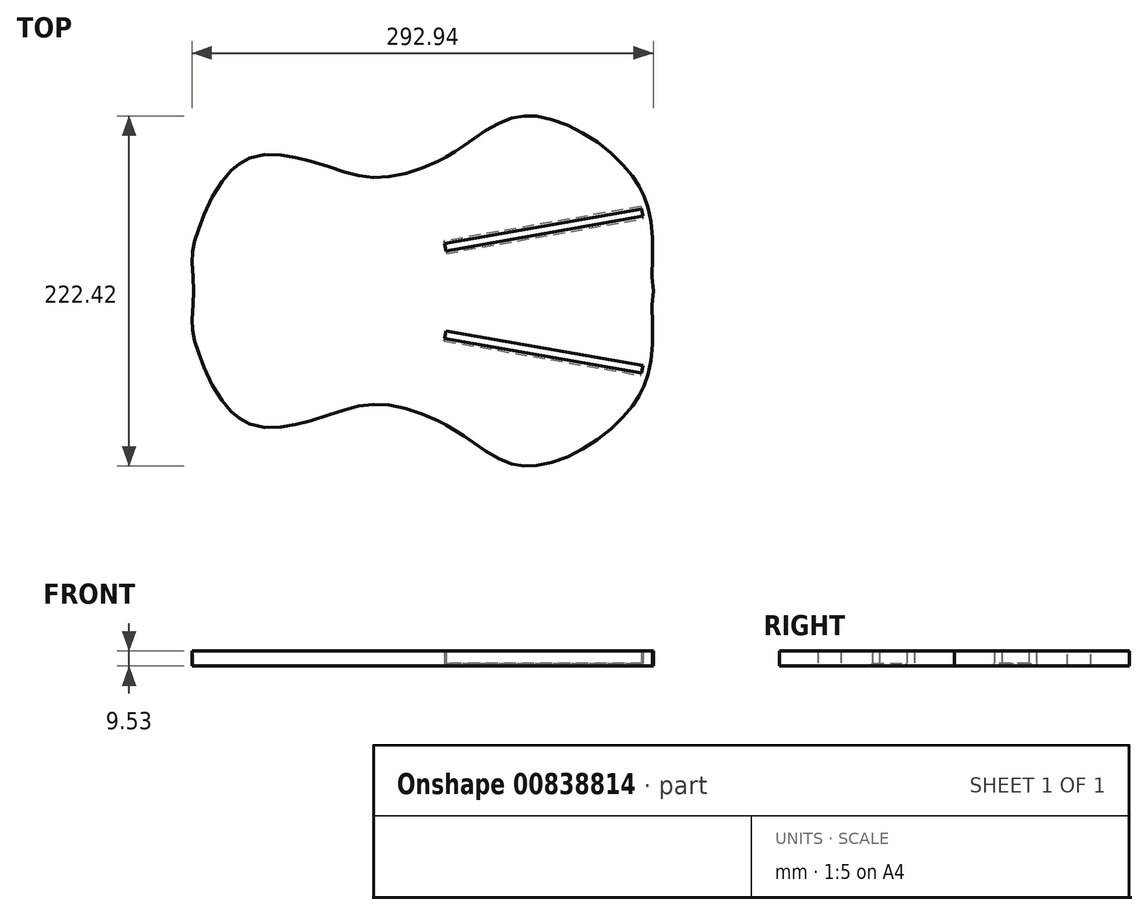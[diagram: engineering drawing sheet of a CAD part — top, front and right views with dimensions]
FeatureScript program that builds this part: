
annotation { "Feature Type Name" : "Feature", "Feature Type Description" : "" }
export const myFeature = defineFeature(function(context is Context, id is Id, definition is map)
    precondition{}
    {
        {
            var Q0;
            Q0=qCreatedBy(makeId("Top.planeOp"),FACE);
            var sketch = newSketch(context, id + "F0", { "sketchPlane" : qUnion([Q0])});
            skFitSpline(sketch, "E0.0", {"points": [v(-120.65, 0) * mm, v(-120.65, 2.86) * mm, v(-120.78, 7.78) * mm, v(-121.14, 13.33) * mm, v(-121.46, 17.64) * mm, v(-121.52, 20.68) * mm, v(-121.36, 23.19) * mm, v(-121.13, 25.21) * mm, v(-120.73, 27.5) * mm, v(-120.15, 30.12) * mm, v(-119.4, 33.04) * mm, v(-118.46, 36.2) * mm, v(-117.36, 39.56) * mm, v(-115.68, 44.24) * mm, v(-113.2, 50.35) * mm, v(-109.68, 57.75) * mm, v(-105.67, 64.87) * mm, v(-102, 70.27) * mm, v(-98.9, 74.1) * mm, v(-96.5, 76.7) * mm, v(-94.47, 78.57) * mm, v(-92.83, 79.9) * mm, v(-91.16, 81.11) * mm, v(-89.05, 82.43) * mm, v(-85.6, 84.16) * mm, v(-81.13, 85.67) * mm, v(-75.54, 86.57) * mm, v(-69.76, 86.7) * mm, v(-63.85, 86.21) * mm, v(-58.88, 85.4) * mm, v(-54.92, 84.57) * mm, v(-51, 83.66) * mm, v(-44.2, 81.86) * mm, v(-36.73, 79.5) * mm, v(-29.7, 77.2) * mm, v(-24.7, 75.6) * mm, v(-19.97, 74.2) * mm, v(-15.38, 73.09) * mm, v(-10.74, 72.3) * mm, v(-5.92, 71.95) * mm, v(-0.77, 72.07) * mm, v(4.85, 72.72) * mm, v(10.87, 73.9) * mm, v(17.2, 75.57) * mm, v(23.74, 77.73) * mm, v(30.39, 80.39) * mm, v(35.92, 83) * mm, v(40.3, 85.33) * mm, v(43.54, 87.2) * mm, v(46.72, 89.17) * mm, v(49.83, 91.23) * mm, v(52.87, 93.34) * mm, v(56.87, 96.16) * mm, v(61.79, 99.64) * mm, v(67.68, 103.5) * mm, v(73.66, 106.8) * mm, v(79.84, 109.33) * mm, v(85.24, 110.64) * mm, v(89.81, 111.12) * mm, v(94.57, 111.17) * mm, v(101, 110.4) * mm, v(109.24, 108.22) * mm, v(117.73, 104.9) * mm, v(126.24, 100.58) * mm, v(134.55, 95.38) * mm, v(142.43, 89.43) * mm, v(149.65, 82.9) * mm, v(154.94, 77.07) * mm, v(158.62, 72.27) * mm, v(161.1, 68.6) * mm, v(163.24, 64.92) * mm, v(165.04, 61.22) * mm, v(166.54, 57.47) * mm, v(168.16, 52.43) * mm, v(169.57, 46.04) * mm, v(170.5, 38.28) * mm, v(170.98, 27.85) * mm, v(170.75, 14.8) * mm, v(170.94, 4.63) * mm, v(171.47, -0.34) * mm]});
            skFitSpline(sketch, "E1.0", {"points": [v(-120.65, 0) * mm, v(-120.65, -2.86) * mm, v(-120.78, -7.78) * mm, v(-121.14, -13.33) * mm, v(-121.46, -17.64) * mm, v(-121.52, -20.68) * mm, v(-121.36, -23.19) * mm, v(-121.13, -25.21) * mm, v(-120.73, -27.5) * mm, v(-120.15, -30.12) * mm, v(-119.4, -33.04) * mm, v(-118.46, -36.2) * mm, v(-117.36, -39.56) * mm, v(-115.68, -44.24) * mm, v(-113.2, -50.35) * mm, v(-109.68, -57.75) * mm, v(-105.67, -64.87) * mm, v(-102, -70.27) * mm, v(-98.9, -74.1) * mm, v(-96.5, -76.7) * mm, v(-94.47, -78.57) * mm, v(-92.83, -79.9) * mm, v(-91.16, -81.11) * mm, v(-89.05, -82.43) * mm, v(-85.6, -84.16) * mm, v(-81.13, -85.67) * mm, v(-75.54, -86.57) * mm, v(-69.76, -86.7) * mm, v(-63.85, -86.21) * mm, v(-58.88, -85.4) * mm, v(-54.92, -84.57) * mm, v(-51, -83.66) * mm, v(-44.2, -81.86) * mm, v(-36.73, -79.5) * mm, v(-29.7, -77.2) * mm, v(-24.7, -75.6) * mm, v(-19.97, -74.2) * mm, v(-15.38, -73.09) * mm, v(-10.74, -72.3) * mm, v(-5.92, -71.95) * mm, v(-0.77, -72.07) * mm, v(4.85, -72.72) * mm, v(10.87, -73.9) * mm, v(17.2, -75.57) * mm, v(23.74, -77.73) * mm, v(30.39, -80.39) * mm, v(35.92, -83) * mm, v(40.3, -85.33) * mm, v(43.54, -87.2) * mm, v(46.72, -89.17) * mm, v(49.83, -91.23) * mm, v(52.87, -93.34) * mm, v(56.87, -96.16) * mm, v(61.79, -99.64) * mm, v(67.68, -103.5) * mm, v(73.66, -106.8) * mm, v(79.84, -109.33) * mm, v(85.24, -110.64) * mm, v(89.81, -111.12) * mm, v(94.57, -111.17) * mm, v(101, -110.4) * mm, v(109.24, -108.22) * mm, v(117.73, -104.9) * mm, v(126.24, -100.58) * mm, v(134.55, -95.38) * mm, v(142.43, -89.43) * mm, v(149.65, -82.9) * mm, v(154.94, -77.07) * mm, v(158.62, -72.27) * mm, v(161.1, -68.6) * mm, v(163.24, -64.92) * mm, v(165.04, -61.22) * mm, v(166.54, -57.47) * mm, v(168.16, -52.43) * mm, v(169.57, -46.04) * mm, v(170.5, -38.28) * mm, v(170.98, -27.85) * mm, v(170.75, -14.8) * mm, v(170.94, -4.63) * mm, v(171.47, 0.34) * mm]});
            skLineSegment(sketch, "E2", {"start": v(-46.04, 82.31) * mm, "end": v(-46.04, -82.31) * mm});
            skLineSegment(sketch, "E3", {"start": v(-41.28, -80.9) * mm, "end": v(-41.28, 80.9) * mm});
            skLineSegment(sketch, "E4", {"start": v(34.92, 82.56) * mm, "end": v(34.93, -82.56) * mm});
            skLineSegment(sketch, "E5", {"start": v(39.69, -85.02) * mm, "end": v(39.69, 85.02) * mm});
            skFitSpline(sketch, "E6.trimOffspring", {"points": [v(-120.65, 0) * mm, v(-120.65, -2.86) * mm, v(-120.78, -7.78) * mm, v(-121.14, -13.33) * mm, v(-121.46, -17.64) * mm, v(-121.52, -20.68) * mm, v(-121.36, -23.19) * mm, v(-121.13, -25.21) * mm, v(-120.73, -27.5) * mm, v(-120.15, -30.12) * mm, v(-119.4, -33.04) * mm, v(-118.46, -36.2) * mm, v(-117.36, -39.56) * mm, v(-115.68, -44.24) * mm, v(-113.2, -50.35) * mm, v(-109.68, -57.75) * mm, v(-105.67, -64.87) * mm, v(-102, -70.27) * mm, v(-98.9, -74.1) * mm, v(-96.5, -76.7) * mm, v(-94.47, -78.57) * mm, v(-92.83, -79.9) * mm, v(-91.16, -81.11) * mm, v(-89.05, -82.43) * mm, v(-85.6, -84.16) * mm, v(-81.13, -85.67) * mm, v(-75.54, -86.57) * mm, v(-69.76, -86.7) * mm, v(-63.85, -86.21) * mm, v(-58.88, -85.4) * mm, v(-54.92, -84.57) * mm, v(-51, -83.66) * mm, v(-44.2, -81.86) * mm, v(-36.73, -79.5) * mm, v(-29.7, -77.2) * mm, v(-24.7, -75.6) * mm, v(-19.97, -74.2) * mm, v(-15.38, -73.09) * mm, v(-10.74, -72.3) * mm, v(-5.92, -71.95) * mm, v(-0.77, -72.07) * mm, v(4.85, -72.72) * mm, v(10.87, -73.9) * mm, v(17.2, -75.57) * mm, v(23.74, -77.73) * mm, v(30.39, -80.39) * mm, v(35.92, -83) * mm, v(40.3, -85.33) * mm, v(43.54, -87.2) * mm, v(46.72, -89.17) * mm, v(49.83, -91.23) * mm, v(52.87, -93.34) * mm, v(56.87, -96.16) * mm, v(61.79, -99.64) * mm, v(67.68, -103.5) * mm, v(73.66, -106.8) * mm, v(79.84, -109.33) * mm, v(85.24, -110.64) * mm, v(89.81, -111.12) * mm, v(94.57, -111.17) * mm, v(101, -110.4) * mm, v(109.24, -108.22) * mm, v(117.73, -104.9) * mm, v(126.24, -100.58) * mm, v(134.55, -95.38) * mm, v(142.43, -89.43) * mm, v(149.65, -82.9) * mm, v(154.94, -77.07) * mm, v(158.62, -72.27) * mm, v(161.1, -68.6) * mm, v(163.24, -64.92) * mm, v(165.04, -61.22) * mm, v(166.54, -57.47) * mm, v(168.16, -52.43) * mm, v(169.57, -46.04) * mm, v(170.5, -38.28) * mm, v(170.98, -27.85) * mm, v(170.75, -14.8) * mm, v(170.94, -4.63) * mm, v(171.47, 0.34) * mm]});
            skFitSpline(sketch, "E7.trimOffspring", {"points": [v(-120.65, 0) * mm, v(-120.65, 2.86) * mm, v(-120.78, 7.78) * mm, v(-121.14, 13.33) * mm, v(-121.46, 17.64) * mm, v(-121.52, 20.68) * mm, v(-121.36, 23.19) * mm, v(-121.13, 25.21) * mm, v(-120.73, 27.5) * mm, v(-120.15, 30.12) * mm, v(-119.4, 33.04) * mm, v(-118.46, 36.2) * mm, v(-117.36, 39.56) * mm, v(-115.68, 44.24) * mm, v(-113.2, 50.35) * mm, v(-109.68, 57.75) * mm, v(-105.67, 64.87) * mm, v(-102, 70.27) * mm, v(-98.9, 74.1) * mm, v(-96.5, 76.7) * mm, v(-94.47, 78.57) * mm, v(-92.83, 79.9) * mm, v(-91.16, 81.11) * mm, v(-89.05, 82.43) * mm, v(-85.6, 84.16) * mm, v(-81.13, 85.67) * mm, v(-75.54, 86.57) * mm, v(-69.76, 86.7) * mm, v(-63.85, 86.21) * mm, v(-58.88, 85.4) * mm, v(-54.92, 84.57) * mm, v(-51, 83.66) * mm, v(-44.2, 81.86) * mm, v(-36.73, 79.5) * mm, v(-29.7, 77.2) * mm, v(-24.7, 75.6) * mm, v(-19.97, 74.2) * mm, v(-15.38, 73.09) * mm, v(-10.74, 72.3) * mm, v(-5.92, 71.95) * mm, v(-0.77, 72.07) * mm, v(4.85, 72.72) * mm, v(10.87, 73.9) * mm, v(17.2, 75.57) * mm, v(23.74, 77.73) * mm, v(30.39, 80.39) * mm, v(35.92, 83) * mm, v(40.3, 85.33) * mm, v(43.54, 87.2) * mm, v(46.72, 89.17) * mm, v(49.83, 91.23) * mm, v(52.87, 93.34) * mm, v(56.87, 96.16) * mm, v(61.79, 99.64) * mm, v(67.68, 103.5) * mm, v(73.66, 106.8) * mm, v(79.84, 109.33) * mm, v(85.24, 110.64) * mm, v(89.81, 111.12) * mm, v(94.57, 111.17) * mm, v(101, 110.4) * mm, v(109.24, 108.22) * mm, v(117.73, 104.9) * mm, v(126.24, 100.58) * mm, v(134.55, 95.38) * mm, v(142.43, 89.43) * mm, v(149.65, 82.9) * mm, v(154.94, 77.07) * mm, v(158.62, 72.27) * mm, v(161.1, 68.6) * mm, v(163.24, 64.92) * mm, v(165.04, 61.22) * mm, v(166.54, 57.47) * mm, v(168.16, 52.43) * mm, v(169.57, 46.04) * mm, v(170.5, 38.28) * mm, v(170.98, 27.85) * mm, v(170.75, 14.8) * mm, v(170.94, 4.63) * mm, v(171.47, -0.34) * mm]});
            skLineSegment(sketch, "E8", {"start": v(39.69, -25.4) * mm, "end": v(164.76, -47.45) * mm});
            skLineSegment(sketch, "E9.0", {"start": v(38.86, -30.1) * mm, "end": v(163.93, -52.14) * mm});
            skLineSegment(sketch, "E10", {"start": v(163.93, -52.14) * mm, "end": v(164.76, -47.45) * mm});
            skLineSegment(sketch, "E11", {"start": v(38.86, -30.1) * mm, "end": v(39.69, -25.4) * mm});
            skLineSegment(sketch, "E12.MirrorCS", {"start": v(38.86, 30.1) * mm, "end": v(39.69, 25.4) * mm});
            skLineSegment(sketch, "E13.MirrorCS", {"start": v(163.93, 52.14) * mm, "end": v(164.76, 47.45) * mm});
            skLineSegment(sketch, "E14.MirrorCS", {"start": v(38.86, 30.1) * mm, "end": v(163.93, 52.14) * mm});
            skLineSegment(sketch, "E15.MirrorCS", {"start": v(39.69, 25.4) * mm, "end": v(164.76, 47.45) * mm});
            skSolve(sketch);
        }
        {
            var Q0;
            Q0 = qSketchRegion(id + "F0", true);
            extrude(context, id + "F1", {"entities" : qUnion([Q0]), "depth" : 9.52 * mm, "offsetDistance" : 25.4 * mm});
        }
        {
            var Q0;
            Q0=makeQuery(id+"F1.opExtrude","CAP_EDGE",EDGE,{"disambiguationData":[OSD([sQuery(id+"F0.wireOp",EDGE,"E3")])],"isStart":true});
            var Q1;
            Q1=makeQuery(id+"F1.opExtrude","CAP_EDGE",EDGE,{"disambiguationData":[OSD([sQuery(id+"F0.wireOp",EDGE,"E2")])],"isStart":true});
            var Q2;
            Q2=makeQuery(id+"F1.opExtrude","CAP_EDGE",EDGE,{"disambiguationData":[OSD([sQuery(id+"F0.wireOp",EDGE,"E4")])],"isStart":true});
            var Q3;
            {var subQ0=sQuery(id+"F0.wireOp",EDGE,"E5");Q3=makeQuery(id+"F1.opExtrude","CAP_EDGE",EDGE,{"disambiguationData":[OSD([subQ0]),TDD([makeQuery(id+"F0.imprint","IMPRINT",EDGE,{"disambiguationData":[TD([[makeQuery(id+"F0.imprint","INTERSECT",VERTEX,{"derivedFrom":[subQ0,sQuery(id+"F0.wireOp",EDGE,"E6.trimOffspring")]}),-1.0]])],"derivedFrom":subQ0})])],"isStart":true});}
            var Q4;
            Q4=makeQuery(id+"F1.opExtrude","CAP_EDGE",EDGE,{"disambiguationData":[OSD([sQuery(id+"F0.wireOp",EDGE,"E9.0")])],"isStart":true});
            var Q5;
            {var subQ0=sQuery(id+"F0.wireOp",EDGE,"E5");Q5=makeQuery(id+"F1.opExtrude","CAP_EDGE",EDGE,{"disambiguationData":[OSD([subQ0]),TDD([makeQuery(id+"F0.imprint","IMPRINT",EDGE,{"disambiguationData":[TD([[makeQuery(id+"F0.imprint","INTERSECT",VERTEX,{"derivedFrom":[subQ0,sQuery(id+"F0.wireOp",EDGE,"E8"),sQuery(id+"F0.wireOp",EDGE,"E11")]}),-1.0]])],"derivedFrom":subQ0})])],"isStart":true});}
            var Q6;
            Q6=makeQuery(id+"F1.opExtrude","CAP_EDGE",EDGE,{"disambiguationData":[OSD([sQuery(id+"F0.wireOp",EDGE,"E15.MirrorCS")])],"isStart":true});
            var Q7;
            Q7=makeQuery(id+"F1.opExtrude","CAP_EDGE",EDGE,{"disambiguationData":[OSD([sQuery(id+"F0.wireOp",EDGE,"E14.MirrorCS")])],"isStart":true});
            var Q8;
            {var subQ0=sQuery(id+"F0.wireOp",EDGE,"E5");Q8=makeQuery(id+"F1.opExtrude","CAP_EDGE",EDGE,{"disambiguationData":[OSD([subQ0]),TDD([makeQuery(id+"F0.imprint","IMPRINT",EDGE,{"disambiguationData":[TD([[makeQuery(id+"F0.imprint","INTERSECT",VERTEX,{"derivedFrom":[subQ0,sQuery(id+"F0.wireOp",EDGE,"E7.trimOffspring")]}),1.0]])],"derivedFrom":subQ0})])],"isStart":true});}
            chamfer(context, id + "F2", {"entities" : qUnion([Q0, Q1, Q2, Q3, Q4, Q5, Q6, Q7, Q8]), "width" : 1.59 * mm, "tangentPropagation" : true});
        }
    });
